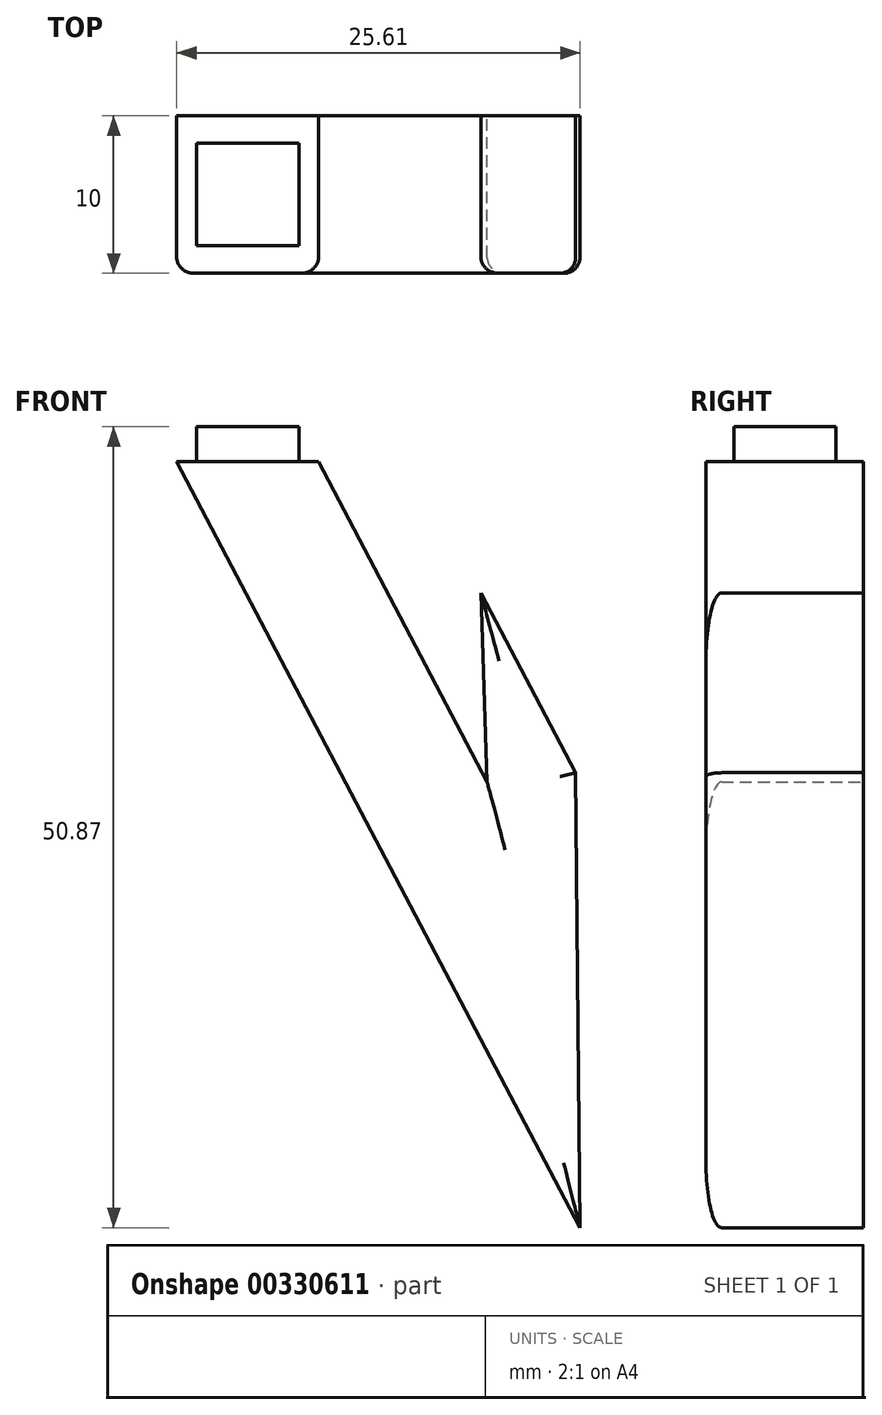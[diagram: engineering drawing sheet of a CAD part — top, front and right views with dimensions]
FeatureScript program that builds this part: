
annotation { "Feature Type Name" : "Feature", "Feature Type Description" : "" }
export const myFeature = defineFeature(function(context is Context, id is Id, definition is map)
    precondition{}
    {
        {
            var Q0;
            Q0=qCreatedBy(makeId("Front.planeOp"),FACE);
            var sketch = newSketch(context, id + "F0", { "sketchPlane" : qUnion([Q0])});
            skLineSegment(sketch, "E0", {"start": v(-25.61, 0) * mm, "end": v(-16.61, 0) * mm});
            skLineSegment(sketch, "E1", {"start": v(-25.61, 0) * mm, "end": v(0, -48.67) * mm});
            skLineSegment(sketch, "E2", {"start": v(0, -48.67) * mm, "end": v(-0.28, -19.77) * mm});
            skLineSegment(sketch, "E3", {"start": v(-0.28, -19.77) * mm, "end": v(-6.29, -8.36) * mm});
            skLineSegment(sketch, "E4", {"start": v(-6.29, -8.36) * mm, "end": v(-5.9, -20.35) * mm});
            skLineSegment(sketch, "E5", {"start": v(-16.61, 0) * mm, "end": v(-5.9, -20.35) * mm});
            skSolve(sketch);
        }
        {
            var Q0;
            Q0=qSketchRegion(id+"F0",true);
            extrude(context, id + "F1", {"entities" : qUnion([Q0]), "depth" : 10 * mm});
        }
        {
            var Q0;
            Q0=makeQuery(id+"F1.opExtrude","CAP_EDGE",EDGE,{"disambiguationData":[OSD([sQuery(id+"F0.wireOp",EDGE,"E1")])],"isStart":false});
            var Q1;
            Q1=makeQuery(id+"F1.opExtrude","CAP_EDGE",EDGE,{"disambiguationData":[OSD([sQuery(id+"F0.wireOp",EDGE,"E5")])],"isStart":false});
            var Q2;
            Q2=makeQuery(id+"F1.opExtrude","CAP_EDGE",EDGE,{"disambiguationData":[OSD([sQuery(id+"F0.wireOp",EDGE,"E4")])],"isStart":false});
            var Q3;
            Q3=makeQuery(id+"F1.opExtrude","CAP_EDGE",EDGE,{"disambiguationData":[OSD([sQuery(id+"F0.wireOp",EDGE,"E3")])],"isStart":false});
            var Q4;
            Q4=makeQuery(id+"F1.opExtrude","CAP_EDGE",EDGE,{"disambiguationData":[OSD([sQuery(id+"F0.wireOp",EDGE,"E2")])],"isStart":false});
            fillet(context, id + "F2", {"entities" : qUnion([Q0, Q1, Q2, Q3, Q4]), "radius" : 1 * mm, "tangentPropagation" : true, "allowEdgeOverflow" : false});
        }
        {
            var Q0;
            Q0=makeQuery(id+"F1.opExtrude","SWEPT_FACE",FACE,{"disambiguationData":[OSD([sQuery(id+"F0.wireOp",EDGE,"E0")])]});
            var sketch = newSketch(context, id + "F3", { "sketchPlane" : qUnion([Q0])});
            skLineSegment(sketch, "E6.bottom", {"start": v(-24.35, -1.75) * mm, "end": v(-17.86, -1.75) * mm});
            skLineSegment(sketch, "E6.top", {"start": v(-24.35, -8.23) * mm, "end": v(-17.86, -8.23) * mm});
            skLineSegment(sketch, "E6.left", {"start": v(-24.35, -1.75) * mm, "end": v(-24.35, -8.23) * mm});
            skLineSegment(sketch, "E6.right", {"start": v(-17.86, -1.75) * mm, "end": v(-17.86, -8.23) * mm});
            skSolve(sketch);
        }
        {
            var Q0;
            Q0=qSketchRegion(id+"F3",true);
            extrude(context, id + "F4", {"entities" : qUnion([Q0]), "operationType" : NewBodyOperationType.ADD, "depth" : 2.2 * mm});
        }
    });
